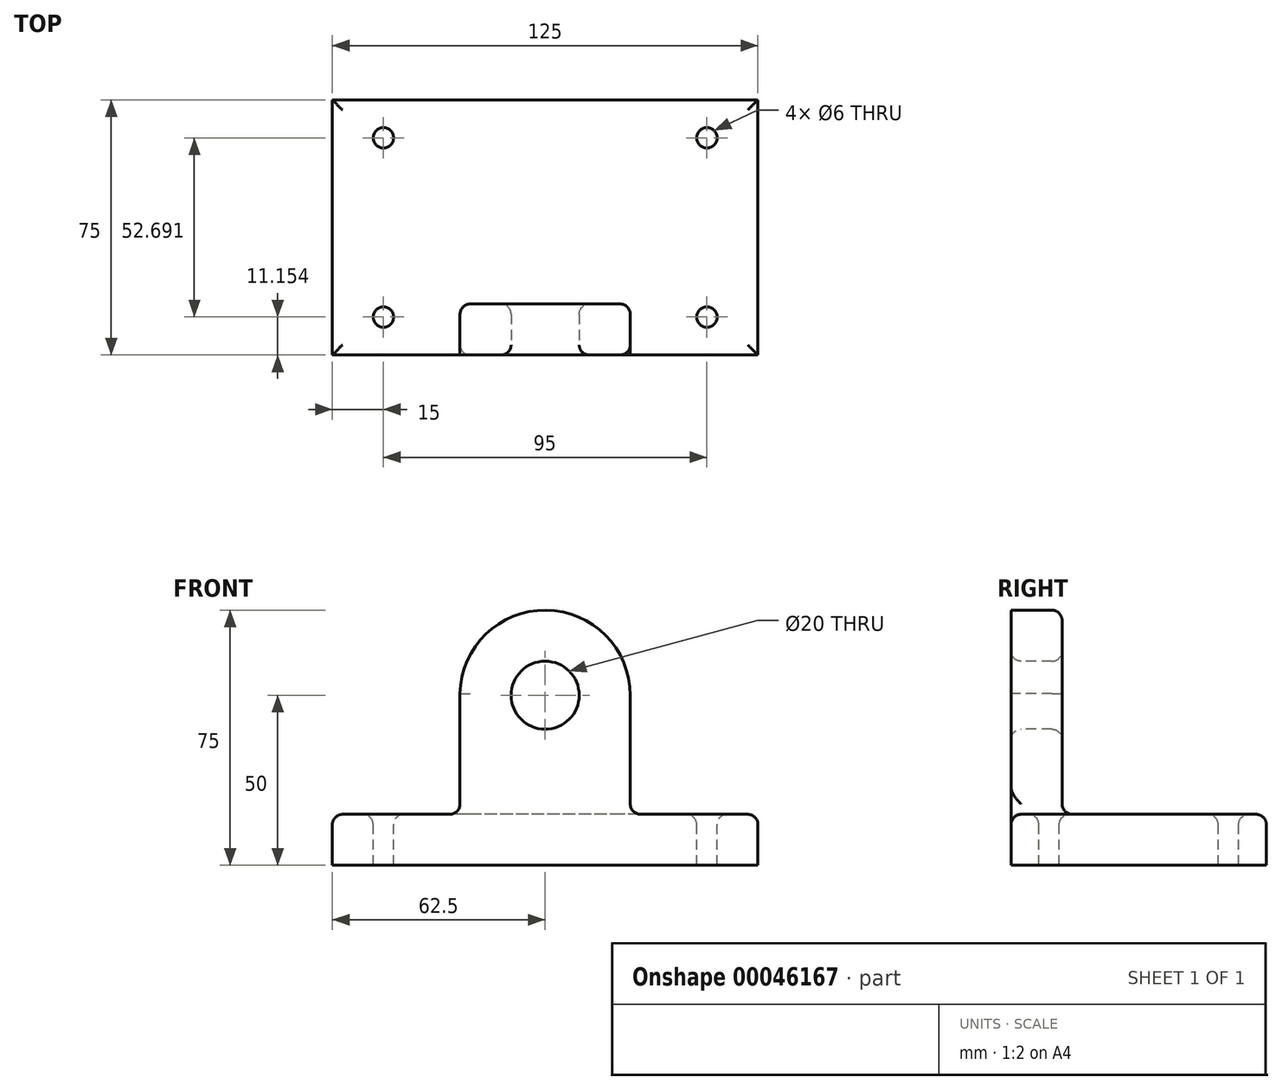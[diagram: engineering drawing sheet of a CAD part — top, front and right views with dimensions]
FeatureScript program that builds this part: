
annotation { "Feature Type Name" : "Feature", "Feature Type Description" : "" }
export const myFeature = defineFeature(function(context is Context, id is Id, definition is map)
    precondition{}
    {
        {
            var Q0;
            Q0=qCreatedBy(makeId("Top.planeOp"),FACE);
            var sketch = newSketch(context, id + "F0", { "sketchPlane" : qUnion([Q0])});
            skLineSegment(sketch, "E0.rect.bottom", {"start": v(62.5, 37.5) * mm, "end": v(-62.5, 37.5) * mm});
            skLineSegment(sketch, "E0.rect.top", {"start": v(62.5, -37.5) * mm, "end": v(-62.5, -37.5) * mm});
            skLineSegment(sketch, "E0.rect.left", {"start": v(62.5, 37.5) * mm, "end": v(62.5, -37.5) * mm});
            skLineSegment(sketch, "E0.rect.right", {"start": v(-62.5, 37.5) * mm, "end": v(-62.5, -37.5) * mm});
            skPoint(sketch, "E0.rect.middle", {"position": v(0, 0) * mm});
            skSolve(sketch);
        }
        {
            var Q0;
            Q0=makeQuery(id+"F0.imprint","IMPRINT",FACE,{"disambiguationData":[TD([[makeQuery(id+"F0.imprint","IMPRINT",EDGE,{"derivedFrom":sQuery(id+"F0.wireOp",EDGE,"E0.rect.bottom")}),1.0]])]});
            extrude(context, id + "F1", {"entities" : qUnion([Q0]), "depth" : 15 * mm});
        }
        {
            var Q0;
            Q0=makeQuery(id+"F1.opExtrude","CAP_FACE",FACE,{"disambiguationData":[OSD([sQuery(id+"F0.wireOp",EDGE,"E0.rect.bottom"),sQuery(id+"F0.wireOp",EDGE,"E0.rect.top"),sQuery(id+"F0.wireOp",EDGE,"E0.rect.left"),sQuery(id+"F0.wireOp",EDGE,"E0.rect.right")])],"isStart":false});
            var sketch = newSketch(context, id + "F2", { "sketchPlane" : qUnion([Q0])});
            skSolve(sketch);
        }
        {
            var Q0;
            Q0=makeQuery(id+"F1.opExtrude","SWEPT_FACE",FACE,{"disambiguationData":[OSD([sQuery(id+"F0.wireOp",EDGE,"E0.rect.top")])]});
            var sketch = newSketch(context, id + "F3", { "sketchPlane" : qUnion([Q0])});
            skLineSegment(sketch, "E1", {"start": v(0, 0) * mm, "end": v(0, 50) * mm, "construction": true});
            skPoint(sketch, "E1.endSnap0", {"position": v(0, 0) * mm});
            skCircle(sketch, "E2", {"center": v(0, 50) * mm, "radius": 25 * mm});
            skLineSegment(sketch, "E3", {"start": v(-25, 50.52) * mm, "end": v(-25, 15) * mm});
            skLineSegment(sketch, "E4", {"start": v(25, 50) * mm, "end": v(25, 15) * mm});
            skLineSegment(sketch, "E5", {"start": v(-25, 15) * mm, "end": v(25, 15) * mm});
            skCircle(sketch, "E6", {"center": v(0, 50) * mm, "radius": 10 * mm});
            skSolve(sketch);
        }
        {
            var Q0;
            {var subQ0=sQuery(id+"F3.wireOp",EDGE,"E4");Q0=makeQuery(id+"F3.imprint","IMPRINT",FACE,{"disambiguationData":[TD([[makeQuery(id+"F3.imprint","IMPRINT",EDGE,{"derivedFrom":subQ0}),-1.0]])]});}
            var Q1;
            {var subQ0=sQuery(id+"F3.wireOp",EDGE,"E3");var subQ1=sQuery(id+"F3.wireOp",EDGE,"E2");var subQ3=makeQuery(id+"F3.imprint","INTERSECT",VERTEX,{"disambiguationData":[OD(0.0)],"derivedFrom":[subQ1,subQ0]});Q1=makeQuery(id+"F3.imprint","IMPRINT",FACE,{"disambiguationData":[TD([[makeQuery(id+"F3.imprint","IMPRINT",EDGE,{"disambiguationData":[TD([[subQ3,1.0]])],"derivedFrom":subQ1}),1.0]])]});}
            extrude(context, id + "F4", {"entities" : qUnion([Q0, Q1]), "operationType" : NewBodyOperationType.ADD, "oppositeDirection" : true, "depth" : 15 * mm});
        }
        {
            var Q0;
            Q0=makeQuery(id+"F2.imprint","IMPRINT",FACE,{"disambiguationData":[TD([[makeQuery(id+"F2.imprint","IMPRINT",EDGE,{"derivedFrom":makeQuery(id+"F1.opExtrude","CAP_EDGE",EDGE,{"disambiguationData":[OSD([sQuery(id+"F0.wireOp",EDGE,"E0.rect.bottom")])],"isStart":false})}),1.0]])]});
            var sketch = newSketch(context, id + "F5", { "sketchPlane" : qUnion([Q0])});
            skLineSegment(sketch, "E7.rect.bottom", {"start": v(47.5, 26.35) * mm, "end": v(-47.5, 26.35) * mm, "construction": true});
            skLineSegment(sketch, "E7.rect.top", {"start": v(47.5, -26.35) * mm, "end": v(-47.5, -26.35) * mm, "construction": true});
            skLineSegment(sketch, "E7.rect.left", {"start": v(47.5, 26.35) * mm, "end": v(47.5, -26.35) * mm, "construction": true});
            skLineSegment(sketch, "E7.rect.right", {"start": v(-47.5, 26.35) * mm, "end": v(-47.5, -26.35) * mm, "construction": true});
            skPoint(sketch, "E7.rect.middle", {"position": v(0, 0) * mm});
            skCircle(sketch, "E8", {"center": v(-47.5, 26.35) * mm, "radius": 3 * mm});
            skCircle(sketch, "E9", {"center": v(47.5, 26.35) * mm, "radius": 3 * mm});
            skCircle(sketch, "E10", {"center": v(47.5, -26.35) * mm, "radius": 3 * mm});
            skCircle(sketch, "E11", {"center": v(-47.5, -26.35) * mm, "radius": 3 * mm});
            skSolve(sketch);
        }
        {
            var Q0;
            Q0 = qSketchRegion(id + "F5", true);
            extrude(context, id + "F6", {"entities" : qUnion([Q0]), "operationType" : NewBodyOperationType.REMOVE, "oppositeDirection" : true, "depth" : 25 * mm});
        }
        {
            var Q0;
            Q0=makeQuery(id+"F1.opExtrude","CAP_FACE",FACE,{"disambiguationData":[OSD([sQuery(id+"F0.wireOp",EDGE,"E0.rect.bottom"),sQuery(id+"F0.wireOp",EDGE,"E0.rect.top"),sQuery(id+"F0.wireOp",EDGE,"E0.rect.left"),sQuery(id+"F0.wireOp",EDGE,"E0.rect.right")])],"isStart":false});
            var Q1;
            Q1=makeQuery(id+"F4.opExtrude","CAP_FACE",FACE,{"disambiguationData":[OSD([sQuery(id+"F3.wireOp",EDGE,"E2"),sQuery(id+"F3.wireOp",EDGE,"E3"),sQuery(id+"F3.wireOp",EDGE,"E4"),sQuery(id+"F3.wireOp",EDGE,"E5"),sQuery(id+"F3.wireOp",EDGE,"E6")])],"isStart":false});
            var Q2;
            Q2=makeQuery(id+"F4.opExtrude","CAP_EDGE",EDGE,{"disambiguationData":[OSD([sQuery(id+"F3.wireOp",EDGE,"E6")])],"isStart":true});
            fillet(context, id + "F7", {"entities" : qUnion([Q0, Q1, Q2]), "radius" : 3 * mm, "tangentPropagation" : true, "allowEdgeOverflow" : false});
        }
    });
